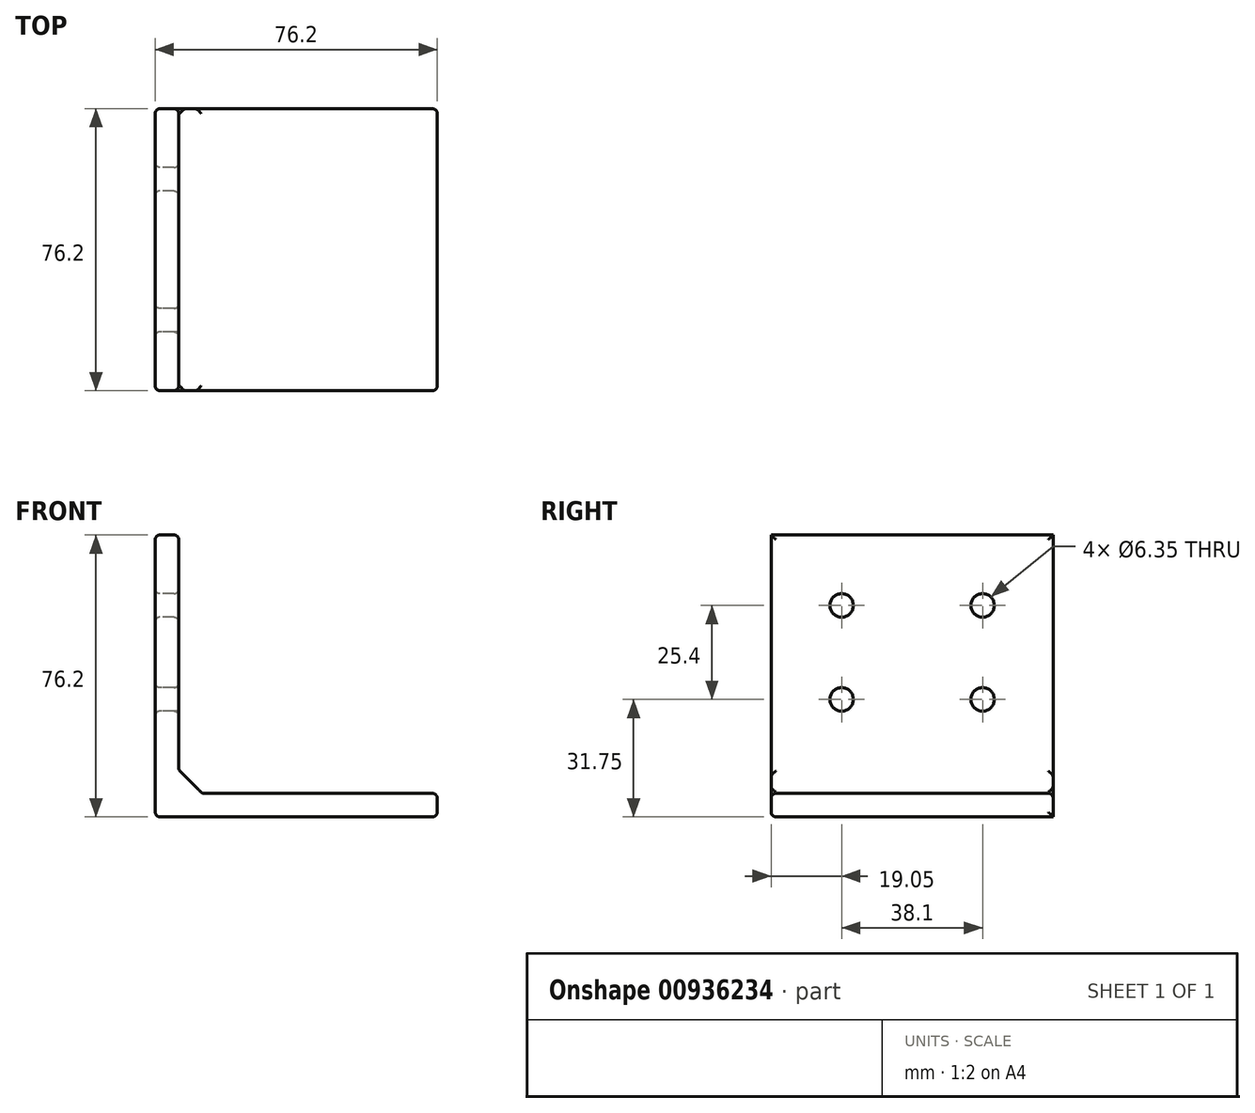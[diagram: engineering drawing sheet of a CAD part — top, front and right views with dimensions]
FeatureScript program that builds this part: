
annotation { "Feature Type Name" : "Feature", "Feature Type Description" : "" }
export const myFeature = defineFeature(function(context is Context, id is Id, definition is map)
    precondition{}
    {
        {
            var Q0;
            Q0=qCreatedBy(makeId("Front.planeOp"),FACE);
            var sketch = newSketch(context, id + "F0", { "sketchPlane" : qUnion([Q0])});
            skLineSegment(sketch, "E0", {"start": v(0, 0) * mm, "end": v(76.2, 0) * mm});
            skLineSegment(sketch, "E1", {"start": v(76.2, 0) * mm, "end": v(76.2, 6.35) * mm});
            skLineSegment(sketch, "E2", {"start": v(76.2, 6.35) * mm, "end": v(6.35, 6.35) * mm});
            skLineSegment(sketch, "E3", {"start": v(6.35, 6.35) * mm, "end": v(6.35, 76.2) * mm});
            skLineSegment(sketch, "E4", {"start": v(6.35, 76.2) * mm, "end": v(0, 76.2) * mm});
            skLineSegment(sketch, "E5", {"start": v(0, 76.2) * mm, "end": v(0, 0) * mm});
            skSolve(sketch);
        }
        {
            var Q0;
            Q0=makeQuery(id+"F0.imprint","IMPRINT",FACE,{"disambiguationData":[TD([[makeQuery(id+"F0.imprint","IMPRINT",EDGE,{"derivedFrom":sQuery(id+"F0.wireOp",EDGE,"E0")}),1.0]])]});
            extrude(context, id + "F1", {"entities" : qUnion([Q0]), "depth" : 76.2 * mm, "offsetDistance" : 25.4 * mm});
        }
        {
            var Q0;
            Q0=makeQuery(id+"F1.opExtrude","SWEPT_EDGE",EDGE,{"disambiguationData":[OSD([sQuery(id+"F0.wireOp",EDGE,"E2"),sQuery(id+"F0.wireOp",EDGE,"E3")])]});
            chamfer(context, id + "F2", {"entities" : qUnion([Q0]), "width" : 6.35 * mm, "tangentPropagation" : true});
        }
        {
            var Q0;
            Q0=makeQuery(id+"F1.opExtrude","SWEPT_FACE",FACE,{"disambiguationData":[OSD([sQuery(id+"F0.wireOp",EDGE,"E5")])]});
            cPlane(context, id + "F3", {"entities" : qUnion([Q0]), "cplaneType" : CPlaneType.OFFSET, "offset" : 0 * mm, "width" : 152.4 * mm, "height" : 152.4 * mm});
        }
        {
            var Q0;
            Q0=qCreatedBy(id+"F3.planeOp",FACE);
            var sketch = newSketch(context, id + "F4", { "sketchPlane" : qUnion([Q0])});
            skCircle(sketch, "E6", {"center": v(19.05, 31.75) * mm, "radius": 3.18 * mm});
            skCircle(sketch, "E7.0.1.0", {"center": v(19.05, 57.15) * mm, "radius": 3.18 * mm});
            skCircle(sketch, "E7.1.0.0", {"center": v(57.15, 31.75) * mm, "radius": 3.18 * mm});
            skCircle(sketch, "E7.1.1.0", {"center": v(57.15, 57.15) * mm, "radius": 3.18 * mm});
            skLineSegment(sketch, "E7.direction1", {"start": v(19.05, 31.75) * mm, "end": v(57.15, 31.75) * mm, "construction": true});
            skLineSegment(sketch, "E7.direction2", {"start": v(19.05, 31.75) * mm, "end": v(19.05, 57.15) * mm, "construction": true});
            skSolve(sketch);
        }
        {
            var Q0;
            Q0=makeQuery(id+"F4.imprint","IMPRINT",FACE,{"disambiguationData":[TD([[makeQuery(id+"F4.imprint","IMPRINT",EDGE,{"derivedFrom":sQuery(id+"F4.wireOp",EDGE,"E7.0.1.0")}),1.0]])]});
            var Q1;
            Q1=makeQuery(id+"F4.imprint","IMPRINT",FACE,{"disambiguationData":[TD([[makeQuery(id+"F4.imprint","IMPRINT",EDGE,{"derivedFrom":sQuery(id+"F4.wireOp",EDGE,"E6")}),1.0]])]});
            var Q2;
            Q2=makeQuery(id+"F4.imprint","IMPRINT",FACE,{"disambiguationData":[TD([[makeQuery(id+"F4.imprint","IMPRINT",EDGE,{"derivedFrom":sQuery(id+"F4.wireOp",EDGE,"E7.1.0.0")}),1.0]])]});
            var Q3;
            Q3=makeQuery(id+"F4.imprint","IMPRINT",FACE,{"disambiguationData":[TD([[makeQuery(id+"F4.imprint","IMPRINT",EDGE,{"derivedFrom":sQuery(id+"F4.wireOp",EDGE,"E7.1.1.0")}),1.0]])]});
            extrude(context, id + "F5", {"entities" : qUnion([Q0, Q1, Q2, Q3]), "operationType" : NewBodyOperationType.REMOVE, "endBound" : BoundingType.THROUGH_ALL, "oppositeDirection" : true, "depth" : 25.4 * mm, "offsetDistance" : 25.4 * mm});
        }
        {
            var Q0;
            Q0=makeQuery(id+"F5.boolean.opBoolean","INTERSECT",EDGE,{"derivedFrom":[makeQuery(id+"F1.opExtrude","SWEPT_FACE",FACE,{"disambiguationData":[OSD([sQuery(id+"F0.wireOp",EDGE,"E3")])]}),makeQuery(id+"F5.opExtrude","SWEPT_FACE",FACE,{"disambiguationData":[OSD([sQuery(id+"F4.wireOp",EDGE,"E7.1.1.0")])]})]});
            var Q1;
            Q1=makeQuery(id+"F5.boolean.opBoolean","INTERSECT",EDGE,{"derivedFrom":[makeQuery(id+"F1.opExtrude","SWEPT_FACE",FACE,{"disambiguationData":[OSD([sQuery(id+"F0.wireOp",EDGE,"E3")])]}),makeQuery(id+"F5.opExtrude","SWEPT_FACE",FACE,{"disambiguationData":[OSD([sQuery(id+"F4.wireOp",EDGE,"E7.0.1.0")])]})]});
            var Q2;
            Q2=makeQuery(id+"F5.boolean.opBoolean","COPY",EDGE,{"derivedFrom":makeQuery(id+"F5.opExtrude","CAP_EDGE",EDGE,{"disambiguationData":[OSD([sQuery(id+"F4.wireOp",EDGE,"E7.1.0.0")])],"isStart":true})});
            var Q3;
            Q3=makeQuery(id+"F5.boolean.opBoolean","INTERSECT",EDGE,{"derivedFrom":[makeQuery(id+"F1.opExtrude","SWEPT_FACE",FACE,{"disambiguationData":[OSD([sQuery(id+"F0.wireOp",EDGE,"E3")])]}),makeQuery(id+"F5.opExtrude","SWEPT_FACE",FACE,{"disambiguationData":[OSD([sQuery(id+"F4.wireOp",EDGE,"E6")])]})]});
            var Q4;
            {var subQ0=sQuery(id+"F0.wireOp",EDGE,"E3");Q4=makeQuery(id+"F2.opChamfer","BLEND_EDGE",EDGE,{"blendedFrom":[makeQuery(id+"F1.opExtrude","SWEPT_EDGE",EDGE,{"disambiguationData":[OSD([sQuery(id+"F0.wireOp",EDGE,"E2"),subQ0])]}),makeQuery(id+"F1.opExtrude","SWEPT_FACE",FACE,{"disambiguationData":[OSD([subQ0])]})],"blendedInto":[makeQuery(id+"F1.opExtrude","SWEPT_FACE",FACE,{"disambiguationData":[OSD([subQ0])]})]});}
            var Q5;
            {var subQ0=sQuery(id+"F0.wireOp",EDGE,"E2");Q5=makeQuery(id+"F2.opChamfer","BLEND_EDGE",EDGE,{"blendedFrom":[makeQuery(id+"F1.opExtrude","SWEPT_EDGE",EDGE,{"disambiguationData":[OSD([subQ0,sQuery(id+"F0.wireOp",EDGE,"E3")])]}),makeQuery(id+"F1.opExtrude","SWEPT_FACE",FACE,{"disambiguationData":[OSD([subQ0])]})],"blendedInto":[makeQuery(id+"F1.opExtrude","SWEPT_FACE",FACE,{"disambiguationData":[OSD([subQ0])]})]});}
            var Q6;
            Q6=makeQuery(id+"F1.opExtrude","SWEPT_EDGE",EDGE,{"disambiguationData":[OSD([sQuery(id+"F0.wireOp",EDGE,"E1"),sQuery(id+"F0.wireOp",EDGE,"E2")])]});
            var Q7;
            Q7=makeQuery(id+"F1.opExtrude","CAP_EDGE",EDGE,{"disambiguationData":[OSD([sQuery(id+"F0.wireOp",EDGE,"E2")])],"isStart":false});
            var Q8;
            Q8=makeQuery(id+"F1.opExtrude","CAP_EDGE",EDGE,{"disambiguationData":[OSD([sQuery(id+"F0.wireOp",EDGE,"E2")])],"isStart":true});
            var Q9;
            Q9=makeQuery(id+"F1.opExtrude","CAP_EDGE",EDGE,{"disambiguationData":[OSD([sQuery(id+"F0.wireOp",EDGE,"E3")])],"isStart":true});
            var Q10;
            Q10=makeQuery(id+"F1.opExtrude","CAP_EDGE",EDGE,{"disambiguationData":[OSD([sQuery(id+"F0.wireOp",EDGE,"E3")])],"isStart":false});
            var Q11;
            Q11=makeQuery(id+"F1.opExtrude","SWEPT_EDGE",EDGE,{"disambiguationData":[OSD([sQuery(id+"F0.wireOp",EDGE,"E3"),sQuery(id+"F0.wireOp",EDGE,"E4")])]});
            var Q12;
            Q12=makeQuery(id+"F1.opExtrude","SWEPT_EDGE",EDGE,{"disambiguationData":[OSD([sQuery(id+"F0.wireOp",EDGE,"E0"),sQuery(id+"F0.wireOp",EDGE,"E1")])]});
            var Q13;
            Q13=makeQuery(id+"F1.opExtrude","CAP_EDGE",EDGE,{"disambiguationData":[OSD([sQuery(id+"F0.wireOp",EDGE,"E1")])],"isStart":false});
            var Q14;
            Q14=makeQuery(id+"F1.opExtrude","CAP_EDGE",EDGE,{"disambiguationData":[OSD([sQuery(id+"F0.wireOp",EDGE,"E1")])],"isStart":true});
            var Q15;
            Q15=makeQuery(id+"F1.opExtrude","CAP_EDGE",EDGE,{"disambiguationData":[OSD([sQuery(id+"F0.wireOp",EDGE,"E0")])],"isStart":false});
            var Q16;
            Q16=makeQuery(id+"F1.opExtrude","CAP_EDGE",EDGE,{"disambiguationData":[OSD([sQuery(id+"F0.wireOp",EDGE,"E5")])],"isStart":false});
            var Q17;
            Q17=makeQuery(id+"F5.boolean.opBoolean","COPY",EDGE,{"derivedFrom":makeQuery(id+"F5.opExtrude","CAP_EDGE",EDGE,{"disambiguationData":[OSD([sQuery(id+"F4.wireOp",EDGE,"E7.0.1.0")])],"isStart":true})});
            var Q18;
            Q18=makeQuery(id+"F5.boolean.opBoolean","COPY",EDGE,{"derivedFrom":makeQuery(id+"F5.opExtrude","CAP_EDGE",EDGE,{"disambiguationData":[OSD([sQuery(id+"F4.wireOp",EDGE,"E7.1.1.0")])],"isStart":true})});
            var Q19;
            Q19=makeQuery(id+"F5.boolean.opBoolean","COPY",EDGE,{"derivedFrom":makeQuery(id+"F5.opExtrude","CAP_EDGE",EDGE,{"disambiguationData":[OSD([sQuery(id+"F4.wireOp",EDGE,"E6")])],"isStart":true})});
            var Q20;
            Q20=makeQuery(id+"F1.opExtrude","SWEPT_FACE",FACE,{"disambiguationData":[OSD([sQuery(id+"F0.wireOp",EDGE,"E5")])]});
            fillet(context, id + "F6", {"entities" : qUnion([Q0, Q1, Q2, Q3, Q4, Q5, Q6, Q7, Q8, Q9, Q10, Q11, Q12, Q13, Q14, Q15, Q16, Q17, Q18, Q19, Q20]), "radius" : 1.27 * mm, "tangentPropagation" : true, "allowEdgeOverflow" : false});
        }
    });
